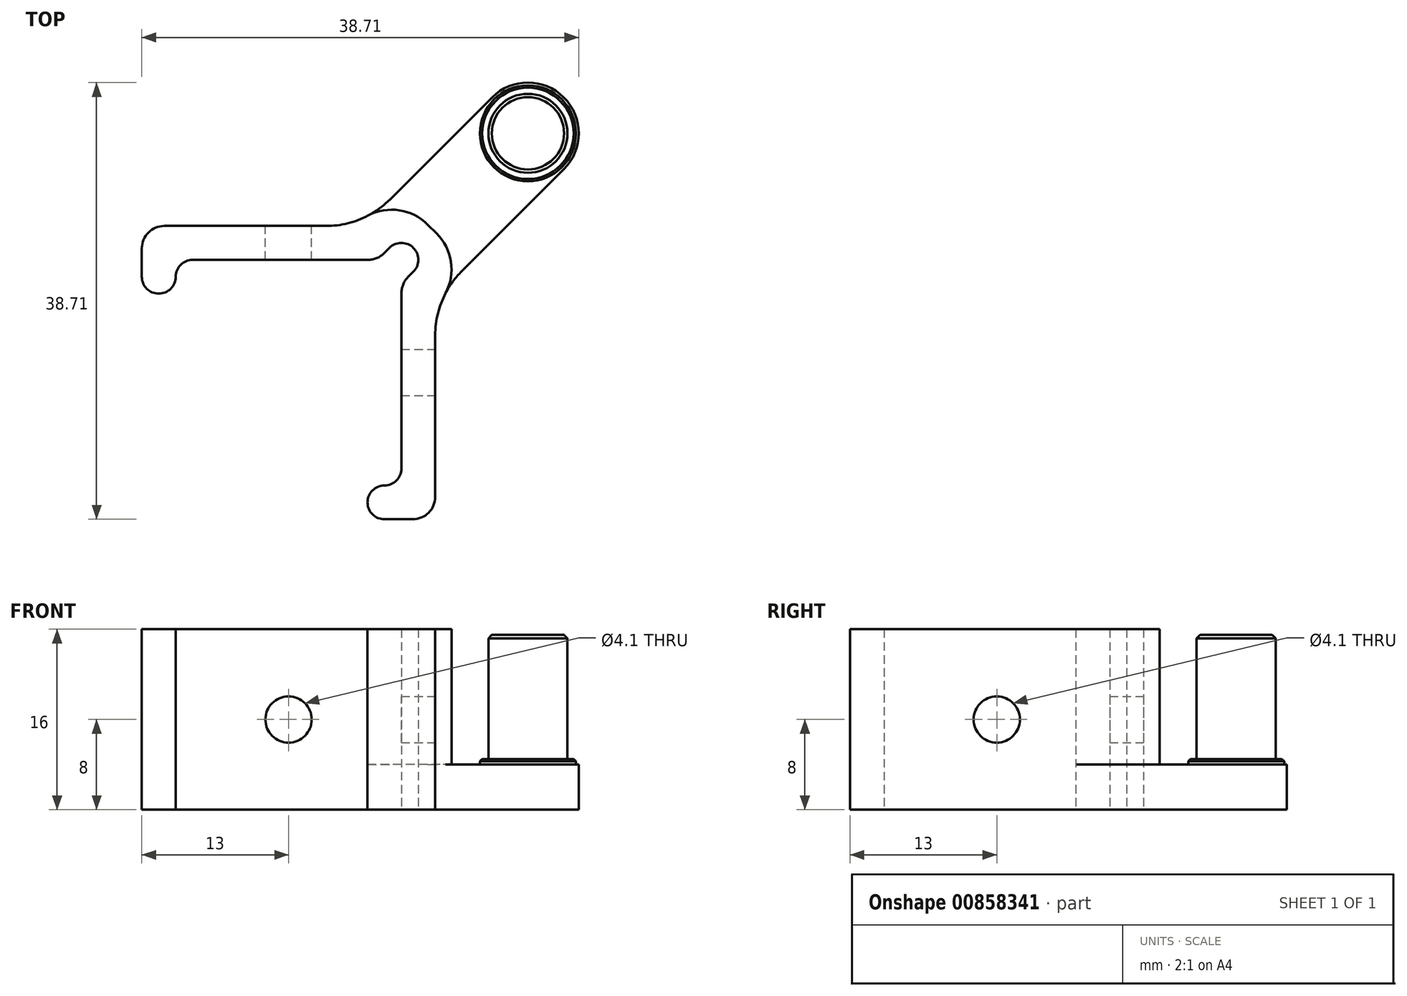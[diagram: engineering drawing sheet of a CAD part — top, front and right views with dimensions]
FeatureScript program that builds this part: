
annotation { "Feature Type Name" : "Feature", "Feature Type Description" : "" }
export const myFeature = defineFeature(function(context is Context, id is Id, definition is map)
    precondition{}
    {
        {
            var Q0;
            Q0=qCreatedBy(makeId("Top.planeOp"),FACE);
            var sketch = newSketch(context, id + "F0", { "sketchPlane" : qUnion([Q0])});
            skLineSegment(sketch, "E0", {"start": v(-8.5, 10) * mm, "end": v(10, 10) * mm, "construction": true});
            skLineSegment(sketch, "E1", {"start": v(10, 7.05) * mm, "end": v(10, -8.5) * mm, "construction": true});
            skLineSegment(sketch, "E2", {"start": v(8.5, -13) * mm, "end": v(11, -13) * mm});
            skLineSegment(sketch, "E3", {"start": v(13, -11) * mm, "end": v(13, 3.32) * mm});
            skLineSegment(sketch, "E4", {"start": v(15.34, 8.98) * mm, "end": v(24.4, 18.03) * mm});
            skLineSegment(sketch, "E5", {"start": v(24.4, 24.4) * mm, "end": v(24.4, 24.4) * mm});
            skLineSegment(sketch, "E6", {"start": v(18.03, 24.4) * mm, "end": v(8.98, 15.34) * mm});
            skLineSegment(sketch, "E7", {"start": v(3.32, 13) * mm, "end": v(-11, 13) * mm});
            skLineSegment(sketch, "E8", {"start": v(10, 10) * mm, "end": v(24.4, 24.4) * mm, "construction": true});
            skLineSegment(sketch, "E9", {"start": v(6.64, 13) * mm, "end": v(13, 6.64) * mm, "construction": true});
            skArc(sketch, "E10.filletArc", {"start": v(-8.5, 10) * mm, "mid": v(-9.56, 9.56) * mm, "end": v(-10, 8.5) * mm});
            skArc(sketch, "E11.filletArc", {"start": v(8.5, -10) * mm, "mid": v(9.56, -9.56) * mm, "end": v(10, -8.5) * mm});
            skLineSegment(sketch, "E12", {"start": v(8.46, 10.59) * mm, "end": v(8.94, 11.06) * mm});
            skArc(sketch, "E13", {"start": v(8.94, 11.06) * mm, "mid": v(11.06, 11.06) * mm, "end": v(11.06, 8.94) * mm});
            skLineSegment(sketch, "E14", {"start": v(11.06, 8.94) * mm, "end": v(10.59, 8.46) * mm});
            skLineSegment(sketch, "E15", {"start": v(-8.5, 10) * mm, "end": v(7.05, 10) * mm});
            skArc(sketch, "E16", {"start": v(-10, 8.5) * mm, "mid": v(-11.5, 7) * mm, "end": v(-13, 8.5) * mm});
            skLineSegment(sketch, "E17", {"start": v(-13, 8.5) * mm, "end": v(-13, 11) * mm});
            skArc(sketch, "E18", {"start": v(8.5, -10) * mm, "mid": v(7, -11.5) * mm, "end": v(8.5, -13) * mm});
            skPoint(sketch, "E19.visualSharp", {"position": v(-13, 13) * mm});
            skArc(sketch, "E19.filletArc", {"start": v(-11, 13) * mm, "mid": v(-12.41, 12.41) * mm, "end": v(-13, 11) * mm});
            skPoint(sketch, "E20.visualSharp", {"position": v(13, -13) * mm});
            skArc(sketch, "E20.filletArc", {"start": v(11, -13) * mm, "mid": v(12.41, -12.41) * mm, "end": v(13, -11) * mm});
            skPoint(sketch, "E21.visualSharp", {"position": v(6.64, 13) * mm});
            skArc(sketch, "E21.filletArc", {"start": v(3.32, 13) * mm, "mid": v(6.38, 13.6) * mm, "end": v(8.98, 15.34) * mm});
            skPoint(sketch, "E22.visualSharp", {"position": v(13, 6.64) * mm});
            skArc(sketch, "E22.filletArc", {"start": v(15.34, 8.98) * mm, "mid": v(13.6, 6.38) * mm, "end": v(13, 3.32) * mm});
            skPoint(sketch, "E23.visualSharp", {"position": v(7.88, 10) * mm});
            skArc(sketch, "E23.filletArc", {"start": v(7.05, 10) * mm, "mid": v(7.82, 10.15) * mm, "end": v(8.46, 10.59) * mm});
            skArc(sketch, "E24.filletArc", {"start": v(10.59, 8.46) * mm, "mid": v(10.15, 7.82) * mm, "end": v(10, 7.05) * mm});
            skLineSegment(sketch, "E25", {"start": v(10, 7.05) * mm, "end": v(10, -8.5) * mm});
            skPoint(sketch, "E26.visualSharp", {"position": v(27.58, 21.21) * mm});
            skArc(sketch, "E26.filletArc", {"start": v(24.4, 18.03) * mm, "mid": v(25.71, 21.21) * mm, "end": v(24.4, 24.4) * mm});
            skPoint(sketch, "E27.visualSharp", {"position": v(21.21, 27.58) * mm});
            skArc(sketch, "E27.filletArc", {"start": v(24.4, 24.4) * mm, "mid": v(21.21, 25.71) * mm, "end": v(18.03, 24.4) * mm});
            skSolve(sketch);
        }
        {
            var Q0;
            Q0 = qSketchRegion(id + "F0", true);
            extrude(context, id + "F1", {"entities" : qUnion([Q0]), "depth" : 4 * mm, "offsetDistance" : 25 * mm});
        }
        {
            var Q0;
            Q0=makeQuery(id+"F1.opExtrude","CAP_FACE",FACE,{"disambiguationData":[OSD([sQuery(id+"F0.wireOp",EDGE,"E2"),sQuery(id+"F0.wireOp",EDGE,"E3"),sQuery(id+"F0.wireOp",EDGE,"E4"),sQuery(id+"F0.wireOp",EDGE,"E6"),sQuery(id+"F0.wireOp",EDGE,"E7"),sQuery(id+"F0.wireOp",EDGE,"E10.filletArc"),sQuery(id+"F0.wireOp",EDGE,"E11.filletArc"),sQuery(id+"F0.wireOp",EDGE,"E12"),sQuery(id+"F0.wireOp",EDGE,"E13"),sQuery(id+"F0.wireOp",EDGE,"E14"),sQuery(id+"F0.wireOp",EDGE,"E15"),sQuery(id+"F0.wireOp",EDGE,"E16"),sQuery(id+"F0.wireOp",EDGE,"E17"),sQuery(id+"F0.wireOp",EDGE,"E18"),sQuery(id+"F0.wireOp",EDGE,"E19.filletArc"),sQuery(id+"F0.wireOp",EDGE,"E20.filletArc"),sQuery(id+"F0.wireOp",EDGE,"E21.filletArc"),sQuery(id+"F0.wireOp",EDGE,"E22.filletArc"),sQuery(id+"F0.wireOp",EDGE,"E23.filletArc"),sQuery(id+"F0.wireOp",EDGE,"E24.filletArc"),sQuery(id+"F0.wireOp",EDGE,"E25"),sQuery(id+"F0.wireOp",EDGE,"E26.filletArc"),sQuery(id+"F0.wireOp",EDGE,"E27.filletArc")])],"isStart":false});
            var sketch = newSketch(context, id + "F2", { "sketchPlane" : qUnion([Q0])});
            skCircle(sketch, "E28", {"center": v(21.21, 21.21) * mm, "radius": 4.25 * mm});
            skSolve(sketch);
        }
        {
            var Q0;
            Q0 = qSketchRegion(id + "F2", true);
            extrude(context, id + "F3", {"entities" : qUnion([Q0]), "operationType" : NewBodyOperationType.ADD, "depth" : 0.5 * mm, "offsetDistance" : 25 * mm});
        }
        {
            var Q0;
            Q0=makeQuery(id+"F3.opExtrude","CAP_EDGE",EDGE,{"disambiguationData":[OSD([sQuery(id+"F2.wireOp",EDGE,"E28")])],"isStart":false});
            chamfer(context, id + "F4", {"entities" : qUnion([Q0]), "width" : 0.2 * mm, "tangentPropagation" : true});
        }
        {
            var Q0;
            Q0=makeQuery(id+"F3.opExtrude","CAP_FACE",FACE,{"disambiguationData":[OSD([sQuery(id+"F2.wireOp",EDGE,"E28")])],"isStart":false});
            var sketch = newSketch(context, id + "F5", { "sketchPlane" : qUnion([Q0])});
            skCircle(sketch, "E29", {"center": v(21.21, 21.21) * mm, "radius": 3.5 * mm});
            skSolve(sketch);
        }
        {
            var Q0;
            Q0 = qSketchRegion(id + "F5", true);
            extrude(context, id + "F6", {"entities" : qUnion([Q0]), "operationType" : NewBodyOperationType.ADD, "depth" : 11 * mm, "offsetDistance" : 25 * mm});
        }
        {
            var Q0;
            Q0=makeQuery(id+"F6.opExtrude","CAP_EDGE",EDGE,{"disambiguationData":[OSD([sQuery(id+"F5.wireOp",EDGE,"E29")])],"isStart":false});
            chamfer(context, id + "F7", {"entities" : qUnion([Q0]), "width" : 0.3 * mm, "tangentPropagation" : true});
        }
        {
            var Q0;
            Q0=makeQuery(id+"F1.opExtrude","CAP_FACE",FACE,{"disambiguationData":[OSD([sQuery(id+"F0.wireOp",EDGE,"E2"),sQuery(id+"F0.wireOp",EDGE,"E3"),sQuery(id+"F0.wireOp",EDGE,"E4"),sQuery(id+"F0.wireOp",EDGE,"E5"),sQuery(id+"F0.wireOp",EDGE,"E6"),sQuery(id+"F0.wireOp",EDGE,"E7"),sQuery(id+"F0.wireOp",EDGE,"E10.filletArc"),sQuery(id+"F0.wireOp",EDGE,"E11.filletArc"),sQuery(id+"F0.wireOp",EDGE,"E12"),sQuery(id+"F0.wireOp",EDGE,"E13"),sQuery(id+"F0.wireOp",EDGE,"E14"),sQuery(id+"F0.wireOp",EDGE,"E15"),sQuery(id+"F0.wireOp",EDGE,"E16"),sQuery(id+"F0.wireOp",EDGE,"E17"),sQuery(id+"F0.wireOp",EDGE,"E18"),sQuery(id+"F0.wireOp",EDGE,"E19.filletArc"),sQuery(id+"F0.wireOp",EDGE,"E20.filletArc"),sQuery(id+"F0.wireOp",EDGE,"E21.filletArc"),sQuery(id+"F0.wireOp",EDGE,"E22.filletArc"),sQuery(id+"F0.wireOp",EDGE,"E23.filletArc"),sQuery(id+"F0.wireOp",EDGE,"E24.filletArc"),sQuery(id+"F0.wireOp",EDGE,"E25")])],"isStart":false});
            var Q1;
            Q1=makeQuery(id+"F1.opExtrude","CAP_FACE",FACE,{"disambiguationData":[OSD([sQuery(id+"F0.wireOp",EDGE,"E2"),sQuery(id+"F0.wireOp",EDGE,"E3"),sQuery(id+"F0.wireOp",EDGE,"E4"),sQuery(id+"F0.wireOp",EDGE,"E5"),sQuery(id+"F0.wireOp",EDGE,"E6"),sQuery(id+"F0.wireOp",EDGE,"E7"),sQuery(id+"F0.wireOp",EDGE,"E10.filletArc"),sQuery(id+"F0.wireOp",EDGE,"E11.filletArc"),sQuery(id+"F0.wireOp",EDGE,"E12"),sQuery(id+"F0.wireOp",EDGE,"E13"),sQuery(id+"F0.wireOp",EDGE,"E14"),sQuery(id+"F0.wireOp",EDGE,"E15"),sQuery(id+"F0.wireOp",EDGE,"E16"),sQuery(id+"F0.wireOp",EDGE,"E17"),sQuery(id+"F0.wireOp",EDGE,"E18"),sQuery(id+"F0.wireOp",EDGE,"E19.filletArc"),sQuery(id+"F0.wireOp",EDGE,"E20.filletArc"),sQuery(id+"F0.wireOp",EDGE,"E21.filletArc"),sQuery(id+"F0.wireOp",EDGE,"E22.filletArc"),sQuery(id+"F0.wireOp",EDGE,"E23.filletArc"),sQuery(id+"F0.wireOp",EDGE,"E24.filletArc"),sQuery(id+"F0.wireOp",EDGE,"E25")])],"isStart":false});
            var sketch = newSketch(context, id + "F8", { "sketchPlane" : qUnion([Q0, Q1])});
            skLineSegment(sketch, "E30.0", {"start": v(3.32, 13) * mm, "end": v(-11, 13) * mm});
            skArc(sketch, "E31.0", {"start": v(-11, 13) * mm, "mid": v(-12.41, 12.41) * mm, "end": v(-13, 11) * mm});
            skLineSegment(sketch, "E32.0", {"start": v(-13, 8.5) * mm, "end": v(-13, 11) * mm});
            skArc(sketch, "E33.0", {"start": v(-10, 8.5) * mm, "mid": v(-11.5, 7) * mm, "end": v(-13, 8.5) * mm});
            skArc(sketch, "E34.0", {"start": v(-8.5, 10) * mm, "mid": v(-9.56, 9.56) * mm, "end": v(-10, 8.5) * mm});
            skLineSegment(sketch, "E35.0", {"start": v(-8.5, 10) * mm, "end": v(7.05, 10) * mm});
            skArc(sketch, "E36.0", {"start": v(7.05, 10) * mm, "mid": v(7.82, 10.15) * mm, "end": v(8.46, 10.59) * mm});
            skArc(sketch, "E37.0", {"start": v(8.94, 11.06) * mm, "mid": v(11.06, 11.06) * mm, "end": v(11.06, 8.94) * mm});
            skLineSegment(sketch, "E38.0", {"start": v(8.46, 10.59) * mm, "end": v(8.94, 11.06) * mm});
            skLineSegment(sketch, "E39.0", {"start": v(11.06, 8.94) * mm, "end": v(10.59, 8.46) * mm});
            skArc(sketch, "E40.0", {"start": v(10.59, 8.46) * mm, "mid": v(10.15, 7.82) * mm, "end": v(10, 7.05) * mm});
            skLineSegment(sketch, "E41.0", {"start": v(10, 7.05) * mm, "end": v(10, -8.5) * mm});
            skArc(sketch, "E42.0", {"start": v(8.5, -10) * mm, "mid": v(9.56, -9.56) * mm, "end": v(10, -8.5) * mm});
            skArc(sketch, "E43.0", {"start": v(8.5, -10) * mm, "mid": v(7, -11.5) * mm, "end": v(8.5, -13) * mm});
            skLineSegment(sketch, "E44.0", {"start": v(8.5, -13) * mm, "end": v(11, -13) * mm});
            skArc(sketch, "E45.0", {"start": v(11, -13) * mm, "mid": v(12.41, -12.41) * mm, "end": v(13, -11) * mm});
            skLineSegment(sketch, "E46.0", {"start": v(13, -11) * mm, "end": v(13, 3.32) * mm});
            skLineSegment(sketch, "E47", {"start": v(12.33, 13.12) * mm, "end": v(13.12, 12.33) * mm});
            skLineSegment(sketch, "E48", {"start": v(0, 0) * mm, "end": v(12.73, 12.73) * mm, "construction": true});
            skArc(sketch, "E49", {"start": v(3.32, 13) * mm, "mid": v(5.24, 13.23) * mm, "end": v(7.05, 13.92) * mm});
            skArc(sketch, "E50", {"start": v(13, 3.32) * mm, "mid": v(13.23, 5.24) * mm, "end": v(13.92, 7.05) * mm});
            skArc(sketch, "E51", {"start": v(7.05, 13.92) * mm, "mid": v(9.82, 14.39) * mm, "end": v(12.33, 13.12) * mm});
            skArc(sketch, "E52", {"start": v(13.12, 12.33) * mm, "mid": v(14.39, 9.82) * mm, "end": v(13.92, 7.05) * mm});
            skSolve(sketch);
        }
        {
            var Q0;
            Q0 = qSketchRegion(id + "F8", true);
            extrude(context, id + "F9", {"entities" : qUnion([Q0]), "operationType" : NewBodyOperationType.ADD, "depth" : 12 * mm, "offsetDistance" : 25 * mm});
        }
        {
            var Q0;
            Q0=makeQuery(id+"F9.boolean.opBoolean","MERGE",FACE,{"derivedFrom":[makeQuery(id+"F1.opExtrude","SWEPT_FACE",FACE,{"disambiguationData":[OSD([sQuery(id+"F0.wireOp",EDGE,"E3")])]}),makeQuery(id+"F9.opExtrude","SWEPT_FACE",FACE,{"disambiguationData":[OSD([sQuery(id+"F8.wireOp",EDGE,"E46.0")])]})]});
            var sketch = newSketch(context, id + "F10", { "sketchPlane" : qUnion([Q0])});
            skPoint(sketch, "E53.middle", {"position": v(0, 8) * mm});
            skSolve(sketch);
        }
        {
            var Q0;
            Q0=makeQuery(id+"F9.boolean.opBoolean","MERGE",FACE,{"derivedFrom":[makeQuery(id+"F1.opExtrude","SWEPT_FACE",FACE,{"disambiguationData":[OSD([sQuery(id+"F0.wireOp",EDGE,"E7")])]}),makeQuery(id+"F9.opExtrude","SWEPT_FACE",FACE,{"disambiguationData":[OSD([sQuery(id+"F8.wireOp",EDGE,"E30.0")])]})]});
            var sketch = newSketch(context, id + "F11", { "sketchPlane" : qUnion([Q0])});
            skPoint(sketch, "E54.middle", {"position": v(0, 8) * mm});
            skSolve(sketch);
        }
        {
            var Q0;
            Q0=sQuery(id+"F11.wireOp",VERTEX,"E54.middle");
            var Q1;
            Q1=sQuery(id+"F10.wireOp",VERTEX,"E53.middle");
            var Q2;
            Q2=makeQuery(id+"F1.opExtrude","SWEPT_BODY",BODY,{"disambiguationData":[OSD([sQuery(id+"F0.wireOp",EDGE,"E2"),sQuery(id+"F0.wireOp",EDGE,"E3"),sQuery(id+"F0.wireOp",EDGE,"E4"),sQuery(id+"F0.wireOp",EDGE,"E6"),sQuery(id+"F0.wireOp",EDGE,"E7"),sQuery(id+"F0.wireOp",EDGE,"E10.filletArc"),sQuery(id+"F0.wireOp",EDGE,"E11.filletArc"),sQuery(id+"F0.wireOp",EDGE,"E12"),sQuery(id+"F0.wireOp",EDGE,"E13"),sQuery(id+"F0.wireOp",EDGE,"E14"),sQuery(id+"F0.wireOp",EDGE,"E15"),sQuery(id+"F0.wireOp",EDGE,"E16"),sQuery(id+"F0.wireOp",EDGE,"E17"),sQuery(id+"F0.wireOp",EDGE,"E18"),sQuery(id+"F0.wireOp",EDGE,"E19.filletArc"),sQuery(id+"F0.wireOp",EDGE,"E20.filletArc"),sQuery(id+"F0.wireOp",EDGE,"E21.filletArc"),sQuery(id+"F0.wireOp",EDGE,"E22.filletArc"),sQuery(id+"F0.wireOp",EDGE,"E23.filletArc"),sQuery(id+"F0.wireOp",EDGE,"E24.filletArc"),sQuery(id+"F0.wireOp",EDGE,"E25"),sQuery(id+"F0.wireOp",EDGE,"E26.filletArc"),sQuery(id+"F0.wireOp",EDGE,"E27.filletArc")])]});
            hole(context, id + "F12", {"style" : HoleStyle.SIMPLE, "endStyle" : HoleEndStyle.THROUGH, "holeDiameter" : 4.1 * mm, "majorDiameter" : 5 * mm, "isTappedThrough" : true, "tappedDepth" : 12 * mm, "tapClearance" : 3, "locations" : qUnion([Q0, Q1]), "scope" : qUnion([Q2])});
        }
    });
